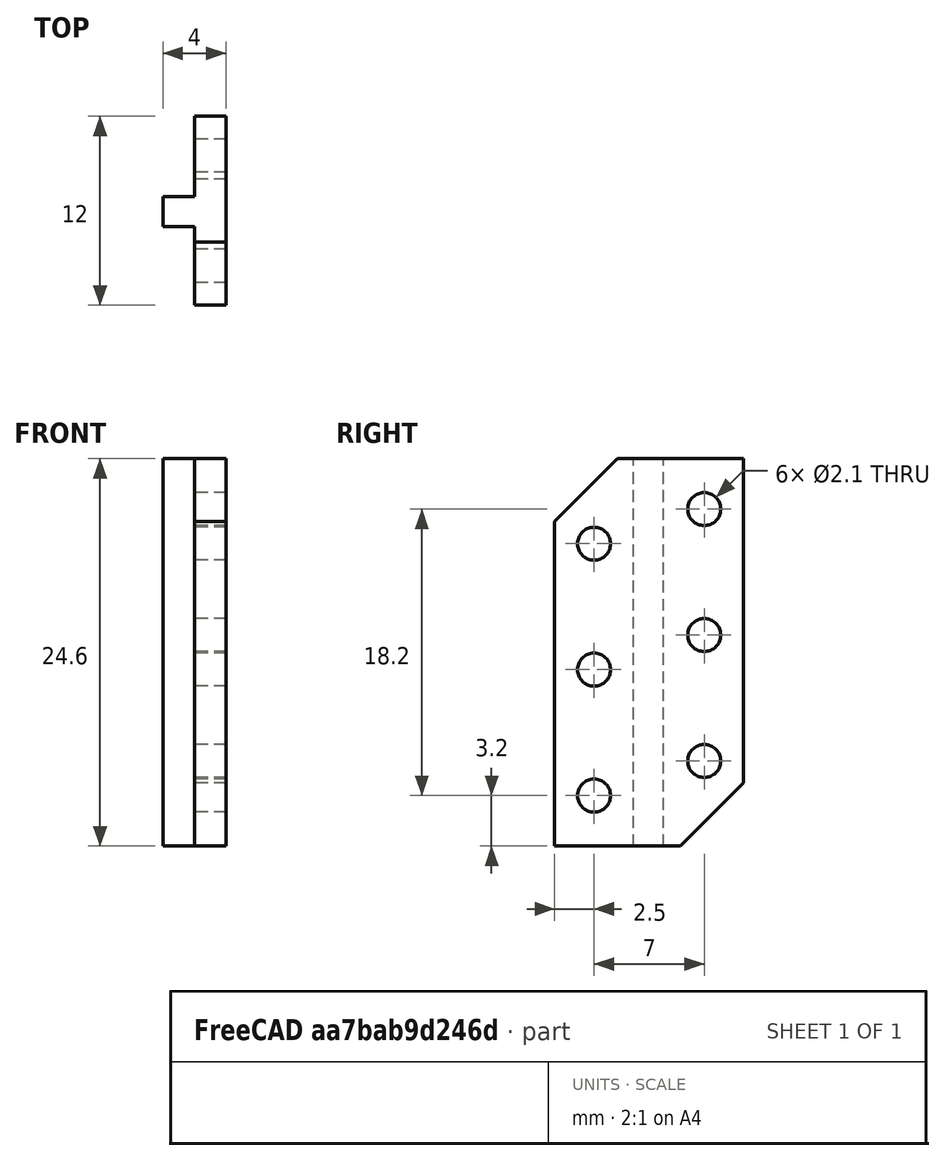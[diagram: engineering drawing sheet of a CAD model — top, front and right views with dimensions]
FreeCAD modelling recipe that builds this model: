
FCSTD DOCUMENT  (FreeCAD 0.15R4671 (Git))
Label: inter_mx-18_fastener
License: CC-BY 3.0
LicenseURL: http://creativecommons.org/licenses/by/3.0/
objects: Part::Cylinder×6, Part::MultiFuse×4, Part::Box×2, Part::Chamfer×2, Part::Cut×1
note: 15 computed .brp shape members not serialized (recipe doc carries the construction recipe); baked Part::Feature solids carry a one-line shape summary decoded from their .brp

FEATURE [Part::Box] Box  label="Cube"
  Height = 2
  Length = 24.6
  Width = 12
FEATURE [Part::Cylinder] Cylinder
  Angle = 360
  Height = 10
  Placement = pos=(0,2.5,-3) rot=(0,0,1;0rad)
  Radius = 1.05
FEATURE [Part::Cylinder] Cylinder001
  Angle = 360
  Height = 10
  Placement = pos=(8,2.5,-3) rot=(0,0,1;0rad)
  Radius = 1.05
FEATURE [Part::Cylinder] Cylinder002
  Angle = 360
  Height = 10
  Placement = pos=(16,2.5,-3) rot=(0,0,1;0rad)
  Radius = 1.05
FEATURE [Part::MultiFuse] Fusion
  Placement = pos=(3.2,0,0) rot=(0,0,1;0rad)
  Shapes = -> [Cylinder,Cylinder002,Cylinder001]
FEATURE [Part::Cylinder] Cylinder003
  Angle = 360
  Height = 10
  Placement = pos=(0,2.5,-3) rot=(0,0,1;0rad)
  Radius = 1.05
FEATURE [Part::Cylinder] Cylinder004
  Angle = 360
  Height = 10
  Placement = pos=(8,2.5,-3) rot=(0,0,1;0rad)
  Radius = 1.05
FEATURE [Part::Cylinder] Cylinder005
  Angle = 360
  Height = 10
  Placement = pos=(16,2.5,-3) rot=(0,0,1;0rad)
  Radius = 1.05
FEATURE [Part::MultiFuse] Fusion001
  Placement = pos=(5.4,7,0) rot=(0,0,1;0rad)
  Shapes = -> [Cylinder003,Cylinder005,Cylinder004]
FEATURE [Part::Box] Box001  label="Cube001"
  Height = 2
  Length = 24.6
  Placement = pos=(0,5,2) rot=(0,0,1;0rad)
  Width = 1.9
FEATURE [Part::MultiFuse] Fusion002
  Shapes = -> [Box001,Box]
FEATURE [Part::MultiFuse] Fusion003
  Shapes = -> [Fusion,Fusion001]
FEATURE [Part::Cut] Cut
  Base = -> Fusion002
  Tool = -> Fusion003
FEATURE [Part::Chamfer] Chamfer
  Base = -> Cut
  Edges = 1 edges r=4: [Edge23]
FEATURE [Part::Chamfer] Chamfer001
  Base = -> Chamfer
  Edges = 1 edges r=4: [Edge34]
  Placement = pos=(0,0,0) rot=(0,-1,0;1.5708rad)
